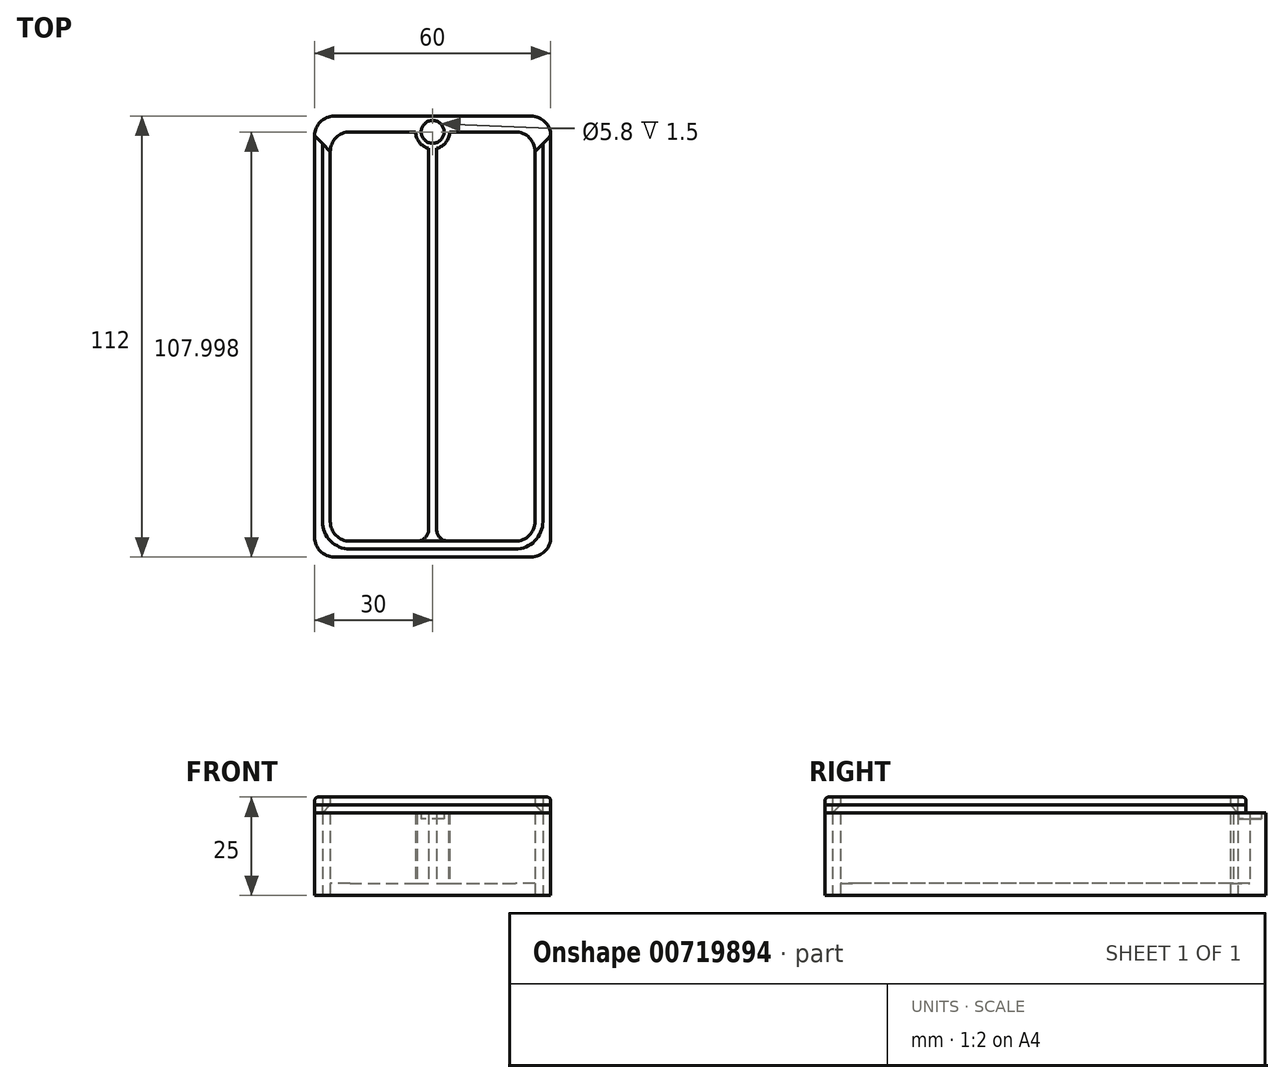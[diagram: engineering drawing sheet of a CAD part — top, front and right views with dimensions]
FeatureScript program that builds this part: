
annotation { "Feature Type Name" : "Feature", "Feature Type Description" : "" }
export const myFeature = defineFeature(function(context is Context, id is Id, definition is map)
    precondition{}
    {
        {
            var Q0;
            Q0=qCreatedBy(makeId("Top.planeOp"),FACE);
            var sketch = newSketch(context, id + "F0", { "sketchPlane" : qUnion([Q0])});
            skLineSegment(sketch, "E0.bottom", {"start": v(-21.75, 48.18) * mm, "end": v(28.25, 48.18) * mm});
            skLineSegment(sketch, "E0.top", {"start": v(-21.75, -63.82) * mm, "end": v(28.25, -63.82) * mm});
            skLineSegment(sketch, "E0.left", {"start": v(-26.75, 43.18) * mm, "end": v(-26.75, -58.82) * mm});
            skLineSegment(sketch, "E0.right", {"start": v(33.25, 43.18) * mm, "end": v(33.25, -58.82) * mm});
            skLineSegment(sketch, "E1.0", {"start": v(-17.75, -59.82) * mm, "end": v(-0.75, -59.82) * mm});
            skLineSegment(sketch, "E1.1", {"start": v(-22.75, 39.18) * mm, "end": v(-22.75, -54.82) * mm});
            skLineSegment(sketch, "E1.2", {"start": v(-17.75, 44.18) * mm, "end": v(-1.05, 44.18) * mm});
            skLineSegment(sketch, "E1.3", {"start": v(29.25, 39.18) * mm, "end": v(29.25, -54.82) * mm});
            skPoint(sketch, "E2.visualSharp", {"position": v(-26.75, 48.18) * mm});
            skArc(sketch, "E2.filletArc", {"start": v(-21.75, 48.18) * mm, "mid": v(-25.29, 46.71) * mm, "end": v(-26.75, 43.18) * mm});
            skPoint(sketch, "E3.visualSharp", {"position": v(-22.75, 44.18) * mm});
            skArc(sketch, "E3.filletArc", {"start": v(-17.75, 44.18) * mm, "mid": v(-21.29, 42.71) * mm, "end": v(-22.75, 39.18) * mm});
            skPoint(sketch, "E4.visualSharp", {"position": v(29.25, 44.18) * mm});
            skArc(sketch, "E4.filletArc", {"start": v(29.25, 39.18) * mm, "mid": v(27.79, 42.71) * mm, "end": v(24.25, 44.18) * mm});
            skPoint(sketch, "E5.visualSharp", {"position": v(33.25, 48.18) * mm});
            skArc(sketch, "E5.filletArc", {"start": v(33.25, 43.18) * mm, "mid": v(31.79, 46.71) * mm, "end": v(28.25, 48.18) * mm});
            skPoint(sketch, "E6.visualSharp", {"position": v(29.25, -59.82) * mm});
            skArc(sketch, "E6.filletArc", {"start": v(24.25, -59.82) * mm, "mid": v(27.79, -58.36) * mm, "end": v(29.25, -54.82) * mm});
            skPoint(sketch, "E7.visualSharp", {"position": v(33.25, -63.82) * mm});
            skArc(sketch, "E7.filletArc", {"start": v(28.25, -63.82) * mm, "mid": v(31.79, -62.36) * mm, "end": v(33.25, -58.82) * mm});
            skPoint(sketch, "E8.visualSharp", {"position": v(-26.75, -63.82) * mm});
            skArc(sketch, "E8.filletArc", {"start": v(-26.75, -58.82) * mm, "mid": v(-25.29, -62.36) * mm, "end": v(-21.75, -63.82) * mm});
            skPoint(sketch, "E9.visualSharp", {"position": v(-22.75, -59.82) * mm});
            skArc(sketch, "E9.filletArc", {"start": v(-22.75, -54.82) * mm, "mid": v(-21.29, -58.36) * mm, "end": v(-17.75, -59.82) * mm});
            skPoint(sketch, "E10", {"position": v(3.25, 44.18) * mm});
            skPoint(sketch, "E11", {"position": v(3.25, -59.82) * mm});
            skCircle(sketch, "E12", {"center": v(3.25, 44.18) * mm, "radius": 2.9 * mm});
            skArc(sketch, "E13.0", {"start": v(1.67, 48.18) * mm, "mid": v(3.25, 39.88) * mm, "end": v(4.83, 48.18) * mm});
            skLineSegment(sketch, "E14.left", {"start": v(2.25, 40) * mm, "end": v(2.25, -56.82) * mm});
            skLineSegment(sketch, "E15.trimOffspring", {"start": v(7.55, 44.18) * mm, "end": v(24.25, 44.18) * mm});
            skLineSegment(sketch, "E16", {"start": v(33.25, 43.18) * mm, "end": v(29.25, 39.18) * mm});
            skLineSegment(sketch, "E17", {"start": v(-26.75, 43.18) * mm, "end": v(-22.75, 39.18) * mm});
            skLineSegment(sketch, "E18.0", {"start": v(31.25, 41.18) * mm, "end": v(31.25, -54.82) * mm});
            skLineSegment(sketch, "E18.1", {"start": v(-24.75, 41.18) * mm, "end": v(-24.75, -54.82) * mm});
            skArc(sketch, "E18.2", {"start": v(-24.75, -54.82) * mm, "mid": v(-22.7, -59.77) * mm, "end": v(-17.75, -61.82) * mm});
            skLineSegment(sketch, "E18.3", {"start": v(-17.75, -61.82) * mm, "end": v(24.25, -61.82) * mm});
            skArc(sketch, "E18.4", {"start": v(24.25, -61.82) * mm, "mid": v(29.2, -59.77) * mm, "end": v(31.25, -54.82) * mm});
            skLineSegment(sketch, "E19", {"start": v(3.25, 44.18) * mm, "end": v(3.25, -59.82) * mm, "construction": true});
            skLineSegment(sketch, "E20.MirrorCS", {"start": v(4.25, 40) * mm, "end": v(4.25, -56.82) * mm});
            skLineSegment(sketch, "E21", {"start": v(-1.05, 44.18) * mm, "end": v(7.55, 44.18) * mm, "construction": true});
            skPoint(sketch, "E22.newPointA", {"position": v(2.25, -59.82) * mm});
            skPoint(sketch, "E22.newPointB", {"position": v(24.25, -59.82) * mm});
            skArc(sketch, "E22.filletArc", {"start": v(-0.75, -59.82) * mm, "mid": v(1.37, -58.94) * mm, "end": v(2.25, -56.82) * mm});
            skLineSegment(sketch, "E23", {"start": v(7.25, -59.82) * mm, "end": v(24.25, -59.82) * mm});
            skPoint(sketch, "E24.visualSharp", {"position": v(4.25, -59.82) * mm});
            skArc(sketch, "E24.filletArc", {"start": v(4.25, -56.82) * mm, "mid": v(5.13, -58.94) * mm, "end": v(7.25, -59.82) * mm});
            skLineSegment(sketch, "E25", {"start": v(-0.75, -59.82) * mm, "end": v(7.25, -59.82) * mm});
            skSolve(sketch);
        }
        {
            var Q0;
            Q0=makeQuery(id+"F0.imprint","IMPRINT",FACE,{"disambiguationData":[TD([[makeQuery(id+"F0.imprint","IMPRINT",EDGE,{"derivedFrom":sQuery(id+"F0.wireOp",EDGE,"E14.top")}),1.0]])]});
            var Q1;
            {var subQ2=sQuery(id+"F0.wireOp",EDGE,"E1.2");var subQ6=sQuery(id+"F0.wireOp",EDGE,"E12");var subQ7=makeQuery(id+"F0.imprint","INTERSECT",VERTEX,{"derivedFrom":[subQ2,subQ6]});Q1=makeQuery(id+"F0.imprint","IMPRINT",FACE,{"disambiguationData":[TD([[makeQuery(id+"F0.imprint","IMPRINT",EDGE,{"disambiguationData":[TD([[subQ7,1.0]])],"derivedFrom":subQ2}),1.0]])]});}
            var Q2;
            {var subQ1=sQuery(id+"F0.wireOp",EDGE,"E4.filletArc");Q2=makeQuery(id+"F0.imprint","IMPRINT",FACE,{"disambiguationData":[TD([[makeQuery(id+"F0.imprint","IMPRINT",EDGE,{"derivedFrom":subQ1}),-1.0]])]});}
            var Q3;
            {var subQ1=sQuery(id+"F0.wireOp",EDGE,"E2.filletArc");Q3=makeQuery(id+"F0.imprint","IMPRINT",FACE,{"disambiguationData":[TD([[makeQuery(id+"F0.imprint","IMPRINT",EDGE,{"derivedFrom":subQ1}),1.0]])]});}
            var Q4;
            {var subQ0=sQuery(id+"F0.wireOp",EDGE,"E14.left");Q4=makeQuery(id+"F0.imprint","IMPRINT",FACE,{"disambiguationData":[TD([[makeQuery(id+"F0.imprint","IMPRINT",EDGE,{"derivedFrom":subQ0}),1.0]])]});}
            var Q5;
            Q5=makeQuery(id+"F0.imprint","IMPRINT",FACE,{"disambiguationData":[TD([[makeQuery(id+"F0.imprint","IMPRINT",EDGE,{"derivedFrom":sQuery(id+"F0.wireOp",EDGE,"E12")}),-1.0]])]});
            extrude(context, id + "F1", {"entities" : qUnion([Q0, Q1, Q2, Q3, Q4, Q5]), "depth" : 21 * mm, "offsetDistance" : 25 * mm});
        }
        {
            var Q0;
            Q0=makeQuery(id+"F0.imprint","IMPRINT",FACE,{"disambiguationData":[TD([[makeQuery(id+"F0.imprint","IMPRINT",EDGE,{"derivedFrom":sQuery(id+"F0.wireOp",EDGE,"E1.1")}),1.0]])]});
            var Q1;
            Q1=makeQuery(id+"F0.imprint","IMPRINT",FACE,{"disambiguationData":[TD([[makeQuery(id+"F0.imprint","IMPRINT",EDGE,{"derivedFrom":sQuery(id+"F0.wireOp",EDGE,"E1.3")}),-1.0]])]});
            extrude(context, id + "F2", {"entities" : qUnion([Q0, Q1]), "operationType" : NewBodyOperationType.ADD, "depth" : 3 * mm, "offsetDistance" : 25 * mm});
        }
        {
            var Q0;
            {var subQ0=sQuery(id+"F0.wireOp",EDGE,"E12");var subQ1=makeQuery(id+"F0.imprint","INTERSECT",VERTEX,{"derivedFrom":[sQuery(id+"F0.wireOp",EDGE,"E1.2"),subQ0]});Q0=makeQuery(id+"F0.imprint","IMPRINT",FACE,{"disambiguationData":[TD([[makeQuery(id+"F0.imprint","IMPRINT",EDGE,{"disambiguationData":[TD([[subQ1,1.0]])],"derivedFrom":subQ0}),1.0]])]});}
            extrude(context, id + "F3", {"entities" : qUnion([Q0]), "operationType" : NewBodyOperationType.ADD, "depth" : 19.5 * mm, "offsetDistance" : 25 * mm});
        }
        {
            var Q0;
            Q0=makeQuery(id+"F0.imprint","IMPRINT",FACE,{"disambiguationData":[TD([[makeQuery(id+"F0.imprint","IMPRINT",EDGE,{"derivedFrom":sQuery(id+"F0.wireOp",EDGE,"E0.top")}),1.0]])]});
            extrude(context, id + "F4", {"entities" : qUnion([Q0]), "operationType" : NewBodyOperationType.ADD, "depth" : 25 * mm, "offsetDistance" : 25 * mm});
        }
        {
            var Q0;
            {var subQ2=sQuery(id+"F0.wireOp",EDGE,"E1.1");Q0=makeQuery(id+"F0.imprint","IMPRINT",FACE,{"disambiguationData":[TD([[makeQuery(id+"F0.imprint","IMPRINT",EDGE,{"derivedFrom":subQ2}),-1.0]])]});}
            extrude(context, id + "F5", {"entities" : qUnion([Q0]), "depth" : 25 * mm, "offsetDistance" : 25 * mm});
        }
        {
            var Q0;
            Q0=qCreatedBy(makeId("Right.planeOp"),FACE);
            var sketch = newSketch(context, id + "F6", { "sketchPlane" : qUnion([Q0])});
            skLineSegment(sketch, "E26.bottom", {"start": v(-87.03, 23) * mm, "end": v(62.97, 23) * mm});
            skLineSegment(sketch, "E26.top", {"start": v(-87.03, 21) * mm, "end": v(62.97, 21) * mm});
            skLineSegment(sketch, "E26.left", {"start": v(-87.03, 23) * mm, "end": v(-87.03, 21) * mm});
            skLineSegment(sketch, "E26.right", {"start": v(62.97, 23) * mm, "end": v(62.97, 21) * mm});
            skSolve(sketch);
        }
        {
            var Q0;
            Q0 = qSketchRegion(id + "F6", true);
            extrude(context, id + "F7", {"entities" : qUnion([Q0]), "operationType" : NewBodyOperationType.REMOVE, "endBound" : BoundingType.SYMMETRIC, "depth" : 70 * mm, "offsetDistance" : 25 * mm});
        }
        {
            var Q0;
            Q0=makeQuery(id+"F7.boolean.opBoolean","COPY",FACE,{"derivedFrom":makeQuery(id+"F7.opExtrude","SWEPT_FACE",FACE,{"disambiguationData":[OSD([sQuery(id+"F6.wireOp",EDGE,"E26.bottom")])]})});
            extrude(context, id + "F8", {"entities" : qUnion([Q0]), "depth" : 2 * mm, "offsetDistance" : 25 * mm});
        }
        {
            var Q0;
            Q0=makeQuery(id+"F8.opExtrude","CAP_EDGE",EDGE,{"disambiguationData":[OSD([sQuery(id+"F0.wireOp",EDGE,"E1.3"),sQuery(id+"F6.wireOp",EDGE,"E26.bottom")])],"isStart":false});
            var Q1;
            Q1=makeQuery(id+"F8.opExtrude","CAP_EDGE",EDGE,{"disambiguationData":[OSD([sQuery(id+"F0.wireOp",EDGE,"E6.filletArc"),sQuery(id+"F6.wireOp",EDGE,"E26.bottom")])],"isStart":false});
            var Q2;
            Q2=makeQuery(id+"F8.opExtrude","CAP_EDGE",EDGE,{"disambiguationData":[OSD([sQuery(id+"F0.wireOp",EDGE,"E1.0"),sQuery(id+"F0.wireOp",EDGE,"E14.top"),sQuery(id+"F6.wireOp",EDGE,"E26.bottom")])],"isStart":false});
            var Q3;
            Q3=makeQuery(id+"F8.opExtrude","CAP_EDGE",EDGE,{"disambiguationData":[OSD([sQuery(id+"F0.wireOp",EDGE,"E9.filletArc"),sQuery(id+"F6.wireOp",EDGE,"E26.bottom")])],"isStart":false});
            var Q4;
            Q4=makeQuery(id+"F8.opExtrude","CAP_EDGE",EDGE,{"disambiguationData":[OSD([sQuery(id+"F0.wireOp",EDGE,"E1.1"),sQuery(id+"F6.wireOp",EDGE,"E26.bottom")])],"isStart":false});
            chamfer(context, id + "F9", {"entities" : qUnion([Q0, Q1, Q2, Q3, Q4]), "width" : 2 * mm, "tangentPropagation" : true});
        }
        {
            var Q0;
            Q0=makeQuery(id+"F4.opExtrude","CAP_EDGE",EDGE,{"disambiguationData":[OSD([sQuery(id+"F0.wireOp",EDGE,"E0.right")])],"isStart":false});
            fillet(context, id + "F10", {"entities" : qUnion([Q0]), "radius" : 1 * mm, "tangentPropagation" : true, "allowEdgeOverflow" : false});
        }
    });
